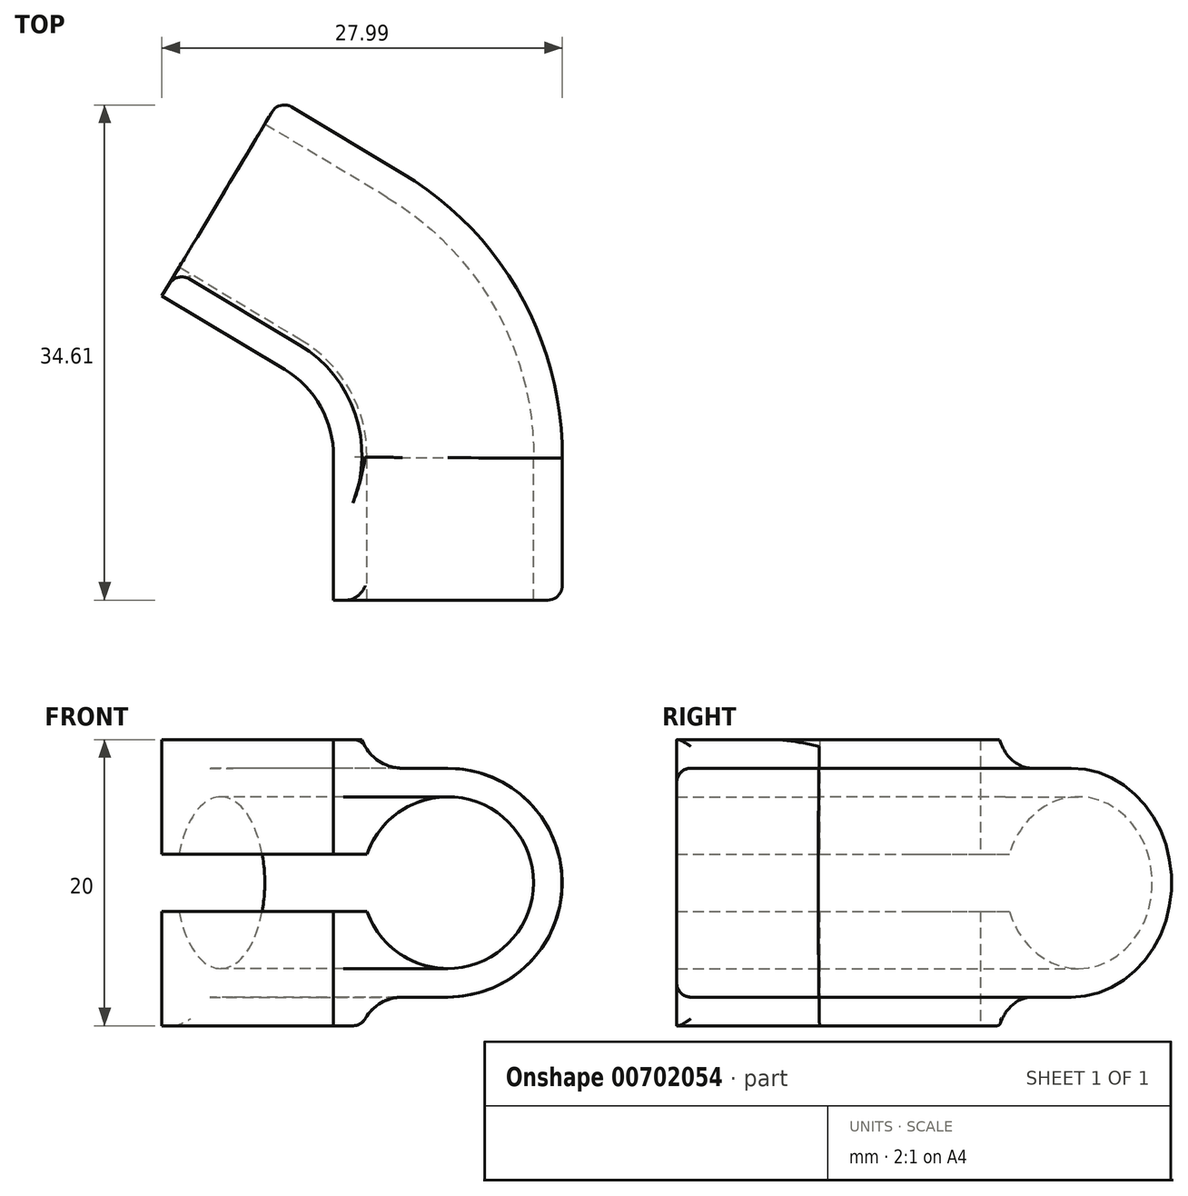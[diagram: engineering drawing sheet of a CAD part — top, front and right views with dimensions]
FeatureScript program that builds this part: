
annotation { "Feature Type Name" : "Feature", "Feature Type Description" : "" }
export const myFeature = defineFeature(function(context is Context, id is Id, definition is map)
    precondition{}
    {
        {
            var Q0;
            Q0=qCreatedBy(makeId("Top.planeOp"),FACE);
            var sketch = newSketch(context, id + "F0", { "sketchPlane" : qUnion([Q0])});
            skLineSegment(sketch, "E0", {"start": v(7, -0.1) * mm, "end": v(7, -10.1) * mm});
            skArc(sketch, "E1", {"start": v(7, -0.1) * mm, "mid": v(6.12, 3.4) * mm, "end": v(3.6, 6) * mm});
            skLineSegment(sketch, "E2", {"start": v(0, 0) * mm, "end": v(3.6, 6) * mm, "construction": true});
            skLineSegment(sketch, "E3", {"start": v(0, 0) * mm, "end": v(7, -0.1) * mm, "construction": true});
            skLineSegment(sketch, "E4", {"start": v(3.6, 6) * mm, "end": v(-4.99, 11.14) * mm});
            skSolve(sketch);
        }
        {
            var Q0;
            Q0=sQuery(id+"F0.wireOp",VERTEX,"E0.end");
            var Q1;
            Q1=qCreatedBy(makeId("Front.planeOp"),FACE);
            cPlane(context, id + "F1", {"entities" : qUnion([Q0, Q1]), "cplaneType" : CPlaneType.PLANE_POINT, "offset" : 25 * mm, "width" : 150 * mm, "height" : 150 * mm});
        }
        {
            var Q0;
            Q0=qCreatedBy(id+"F1.planeOp",FACE);
            var sketch = newSketch(context, id + "F2", { "sketchPlane" : qUnion([Q0])});
            skLineSegment(sketch, "E5", {"start": v(7, 10) * mm, "end": v(7, 2) * mm});
            skLineSegment(sketch, "E6", {"start": v(7, 0) * mm, "end": v(15, 0) * mm, "construction": true});
            skArc(sketch, "E7", {"start": v(15, -8) * mm, "mid": v(23, 0) * mm, "end": v(15, 8) * mm});
            skArc(sketch, "E8", {"start": v(9.34, -2) * mm, "mid": v(21, 0) * mm, "end": v(9.34, 2) * mm});
            skLineSegment(sketch, "E9", {"start": v(15, 0) * mm, "end": v(15, -8) * mm, "construction": true});
            skLineSegment(sketch, "E10.MirrorCS", {"start": v(15, 0) * mm, "end": v(15, 8) * mm, "construction": true});
            skLineSegment(sketch, "E11", {"start": v(15, -8) * mm, "end": v(9, -8) * mm});
            skLineSegment(sketch, "E12", {"start": v(7, -10) * mm, "end": v(9, -10) * mm});
            skLineSegment(sketch, "E13", {"start": v(9, -10) * mm, "end": v(9, -8) * mm});
            skLineSegment(sketch, "E14.MirrorCS", {"start": v(15, 8) * mm, "end": v(9, 8) * mm});
            skLineSegment(sketch, "E15.MirrorCS", {"start": v(9, 10) * mm, "end": v(9, 8) * mm});
            skLineSegment(sketch, "E16.MirrorCS", {"start": v(7, 10) * mm, "end": v(9, 10) * mm});
            skLineSegment(sketch, "E17.bottom", {"start": v(7, 2) * mm, "end": v(9.34, 2) * mm});
            skLineSegment(sketch, "E17.top", {"start": v(7, -2) * mm, "end": v(9.34, -2) * mm});
            skLineSegment(sketch, "E17.left", {"start": v(7, 2) * mm, "end": v(7, 0) * mm});
            skPoint(sketch, "E18.orphan", {"position": v(7, 8) * mm});
            skLineSegment(sketch, "E19.trimOffspring", {"start": v(7, -2) * mm, "end": v(7, -10) * mm});
            skPoint(sketch, "E20.orphan", {"position": v(7, -8) * mm});
            skSolve(sketch);
        }
        {
            var Q0;
            Q0=makeQuery(id+"F2.imprint","IMPRINT",FACE,{"disambiguationData":[TD([[makeQuery(id+"F2.imprint","IMPRINT",EDGE,{"derivedFrom":sQuery(id+"F2.wireOp",EDGE,"E5")}),1.0]])]});
            var Q1;
            Q1=sQuery(id+"F0.wireOp",EDGE,"E0");
            var Q2;
            Q2=sQuery(id+"F0.wireOp",EDGE,"E1");
            var Q3;
            Q3=sQuery(id+"F0.wireOp",EDGE,"E4");
            sweep(context, id + "F3", {"profiles" : qUnion([Q0]), "path" : qUnion([Q1, Q2, Q3])});
        }
        {
            var Q0;
            Q0=makeQuery(id+"F3.opSweep","SWEPT_EDGE",EDGE,{"disambiguationData":[OSD([sQuery(id+"F0.wireOp",EDGE,"b3041f58-c11e-42b4-9d15-3ae8da385f4e"),sQuery(id+"F2.wireOp",EDGE,"E14.MirrorCS"),sQuery(id+"F2.wireOp",EDGE,"E15.MirrorCS")])]});
            var Q1;
            Q1=makeQuery(id+"F3.opSweep","SWEPT_EDGE",EDGE,{"disambiguationData":[OSD([sQuery(id+"F0.wireOp",EDGE,"E0"),sQuery(id+"F2.wireOp",EDGE,"E14.MirrorCS"),sQuery(id+"F2.wireOp",EDGE,"E15.MirrorCS")])]});
            var Q2;
            Q2=makeQuery(id+"F3.opSweep","SWEPT_EDGE",EDGE,{"disambiguationData":[OSD([sQuery(id+"F0.wireOp",EDGE,"E0"),sQuery(id+"F2.wireOp",EDGE,"E11"),sQuery(id+"F2.wireOp",EDGE,"E13")])]});
            fillet(context, id + "F4", {"entities" : qUnion([Q0, Q1, Q2]), "radius" : 3 * mm, "tangentPropagation" : true, "allowEdgeOverflow" : false});
        }
        {
            var Q0;
            {var subQ0=sQuery(id+"F0.wireOp",EDGE,"E0");Q0=makeQuery(id+"F4.opFillet","BLEND_EDGE",EDGE,{"disambiguationData":[OD(0.0)],"blendedFrom":[makeQuery(id+"F3.opSweep","SWEPT_EDGE",EDGE,{"disambiguationData":[OSD([subQ0,sQuery(id+"F2.wireOp",EDGE,"E11"),sQuery(id+"F2.wireOp",EDGE,"E13")])]}),makeQuery(id+"F3.opSweep","SWEPT_FACE",FACE,{"disambiguationData":[OSD([subQ0,sQuery(id+"F2.wireOp",EDGE,"E12")])]})],"blendedInto":[makeQuery(id+"F3.opSweep","SWEPT_FACE",FACE,{"disambiguationData":[OSD([subQ0,sQuery(id+"F2.wireOp",EDGE,"E12")])]})]});}
            var Q1;
            {var subQ0=sQuery(id+"F0.wireOp",EDGE,"E0");Q1=makeQuery(id+"F4.opFillet","BLEND_EDGE",EDGE,{"disambiguationData":[OD(2.0)],"blendedFrom":[makeQuery(id+"F3.opSweep","SWEPT_EDGE",EDGE,{"disambiguationData":[OSD([subQ0,sQuery(id+"F2.wireOp",EDGE,"E11"),sQuery(id+"F2.wireOp",EDGE,"E13")])]}),makeQuery(id+"F3.opSweep","SWEPT_FACE",FACE,{"disambiguationData":[OSD([subQ0,sQuery(id+"F2.wireOp",EDGE,"E12")])]})],"blendedInto":[makeQuery(id+"F3.opSweep","SWEPT_FACE",FACE,{"disambiguationData":[OSD([subQ0,sQuery(id+"F2.wireOp",EDGE,"E12")])]})]});}
            var Q2;
            {var subQ0=sQuery(id+"F0.wireOp",EDGE,"E0");Q2=makeQuery(id+"F4.opFillet","BLEND_EDGE",EDGE,{"blendedFrom":[makeQuery(id+"F3.opSweep","SWEPT_EDGE",EDGE,{"disambiguationData":[OSD([subQ0,sQuery(id+"F2.wireOp",EDGE,"E14.MirrorCS"),sQuery(id+"F2.wireOp",EDGE,"E15.MirrorCS")])]}),makeQuery(id+"F3.opSweep","SWEPT_FACE",FACE,{"disambiguationData":[OSD([subQ0,sQuery(id+"F2.wireOp",EDGE,"E16.MirrorCS")])]})],"blendedInto":[makeQuery(id+"F3.opSweep","SWEPT_FACE",FACE,{"disambiguationData":[OSD([subQ0,sQuery(id+"F2.wireOp",EDGE,"E16.MirrorCS")])]})]});}
            var Q3;
            Q3=makeQuery(id+"F4.opFillet","BLEND_EDGE",EDGE,{"blendedFrom":[makeQuery(id+"F3.opSweep","SWEPT_EDGE",EDGE,{"disambiguationData":[OSD([sQuery(id+"F0.wireOp",EDGE,"b3041f58-c11e-42b4-9d15-3ae8da385f4e"),sQuery(id+"F2.wireOp",EDGE,"E14.MirrorCS"),sQuery(id+"F2.wireOp",EDGE,"E15.MirrorCS")])]}),makeQuery(id+"F3.opSweep","SWEPT_FACE",FACE,{"disambiguationData":[OSD([sQuery(id+"F0.wireOp",EDGE,"E0"),sQuery(id+"F2.wireOp",EDGE,"E16.MirrorCS")])]})],"blendedInto":[makeQuery(id+"F3.opSweep","SWEPT_FACE",FACE,{"disambiguationData":[OSD([sQuery(id+"F0.wireOp",EDGE,"E0"),sQuery(id+"F2.wireOp",EDGE,"E16.MirrorCS")])]})]});
            var Q4;
            Q4=makeQuery(id+"F3.opSweep","CAP_EDGE",EDGE,{"disambiguationData":[OSD([sQuery(id+"F0.wireOp",VERTEX,"gxyRKe71-CtOm-hXhc-hxba-IlVduykBdpom.end"),sQuery(id+"F2.wireOp",EDGE,"E7")])],"isStart":false});
            var Q5;
            Q5=makeQuery(id+"F3.opSweep","CAP_EDGE",EDGE,{"disambiguationData":[OSD([sQuery(id+"F0.wireOp",VERTEX,"E0.end"),sQuery(id+"F2.wireOp",EDGE,"E7")])],"isStart":true});
            fillet(context, id + "F5", {"entities" : qUnion([Q0, Q1, Q2, Q3, Q4, Q5]), "radius" : 1 * mm, "tangentPropagation" : true, "allowEdgeOverflow" : false});
        }
    });
